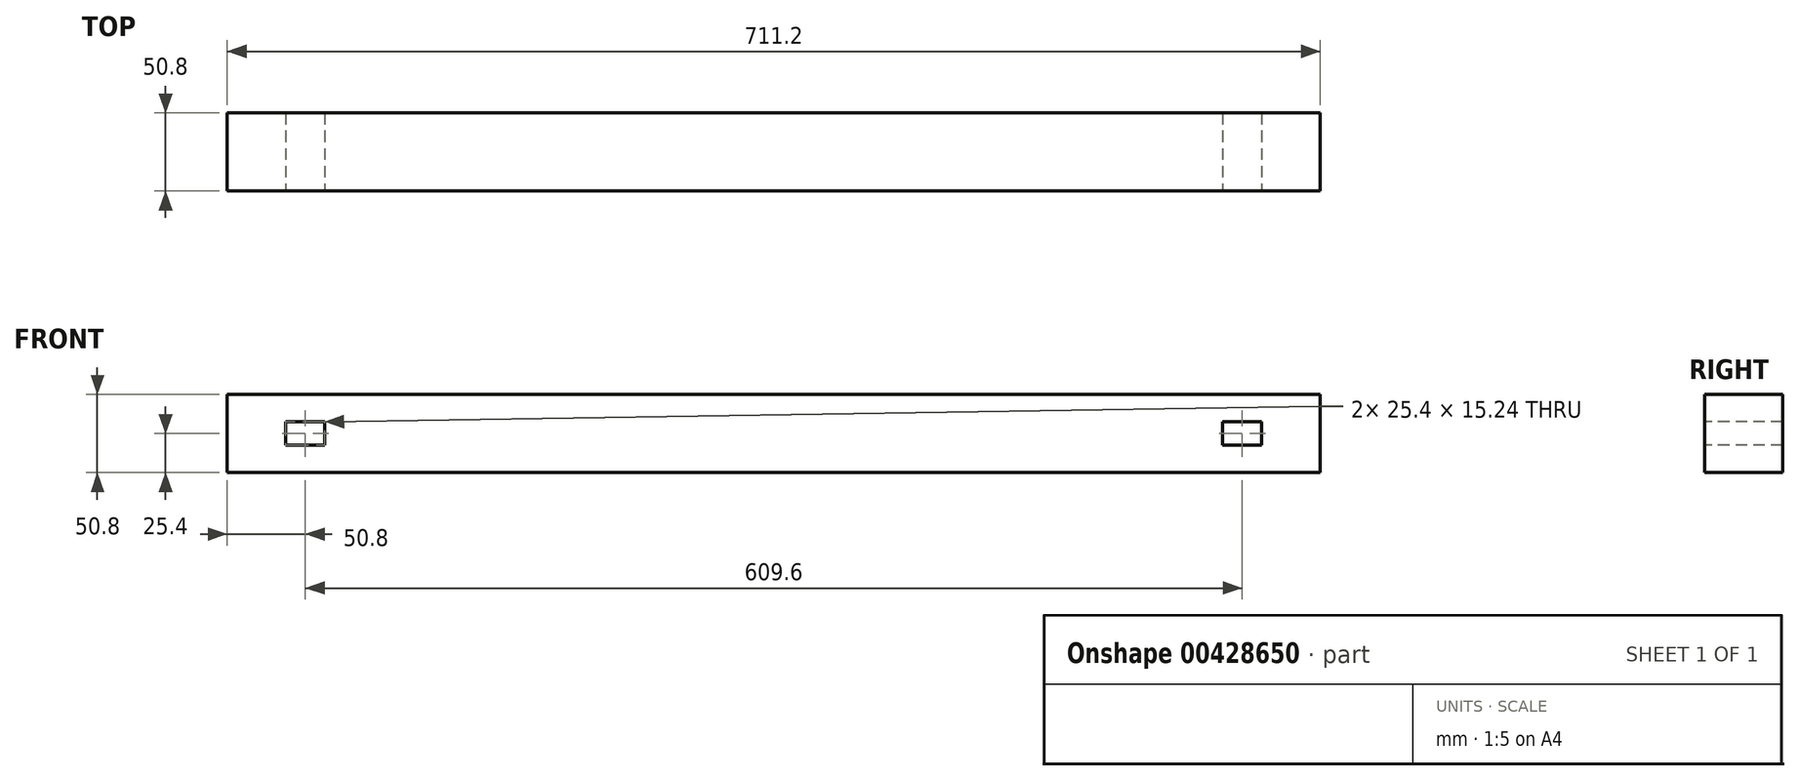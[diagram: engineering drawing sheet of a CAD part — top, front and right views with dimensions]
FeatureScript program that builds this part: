
annotation { "Feature Type Name" : "Feature", "Feature Type Description" : "" }
export const myFeature = defineFeature(function(context is Context, id is Id, definition is map)
    precondition{}
    {
        {
            var Q0;
            Q0=qCreatedBy(makeId("Top.planeOp"),FACE);
            var sketch = newSketch(context, id + "F0", { "sketchPlane" : qUnion([Q0])});
            skLineSegment(sketch, "E0.bottom", {"start": v(-355.6, 25.4) * mm, "end": v(355.6, 25.4) * mm});
            skLineSegment(sketch, "E0.top", {"start": v(-355.6, -25.4) * mm, "end": v(355.6, -25.4) * mm});
            skLineSegment(sketch, "E0.left", {"start": v(-355.6, 25.4) * mm, "end": v(-355.6, -25.4) * mm});
            skLineSegment(sketch, "E0.right", {"start": v(355.6, 25.4) * mm, "end": v(355.6, -25.4) * mm});
            skPoint(sketch, "E0.middle", {"position": v(0, 0) * mm});
            skSolve(sketch);
        }
        {
            var Q0;
            Q0 = qSketchRegion(id + "F0", true);
            extrude(context, id + "F1", {"entities" : qUnion([Q0]), "depth" : 50.8 * mm});
        }
        {
            var Q0;
            Q0=makeQuery(id+"F1.opExtrude","SWEPT_FACE",FACE,{"disambiguationData":[OSD([sQuery(id+"F0.wireOp",EDGE,"E0.top")])]});
            var sketch = newSketch(context, id + "F2", { "sketchPlane" : qUnion([Q0])});
            skLineSegment(sketch, "E1", {"start": v(-355.6, 25.4) * mm, "end": v(-317.5, 25.4) * mm});
            skLineSegment(sketch, "E2", {"start": v(-317.5, 50.8) * mm, "end": v(-317.5, 33.02) * mm});
            skLineSegment(sketch, "E3.bottom", {"start": v(-317.5, 33.02) * mm, "end": v(-292.1, 33.02) * mm});
            skLineSegment(sketch, "E3.top", {"start": v(-317.5, 17.78) * mm, "end": v(-292.1, 17.78) * mm});
            skLineSegment(sketch, "E3.left", {"start": v(-317.5, 33.02) * mm, "end": v(-317.5, 17.78) * mm});
            skLineSegment(sketch, "E3.right", {"start": v(-292.1, 33.02) * mm, "end": v(-292.1, 17.78) * mm});
            skSolve(sketch);
        }
        {
            var Q0;
            Q0 = qSketchRegion(id + "F2", true);
            extrude(context, id + "F3", {"entities" : qUnion([Q0]), "operationType" : NewBodyOperationType.REMOVE, "oppositeDirection" : true, "depth" : 50.8 * mm});
        }
        {
            var Q0;
            Q0=makeQuery(id+"F1.opExtrude","SWEPT_FACE",FACE,{"disambiguationData":[OSD([sQuery(id+"F0.wireOp",EDGE,"E0.top")])]});
            var sketch = newSketch(context, id + "F4", { "sketchPlane" : qUnion([Q0])});
            skPoint(sketch, "E4.endSnap0", {"position": v(355.6, 25.4) * mm});
            skLineSegment(sketch, "E5", {"start": v(355.6, 25.4) * mm, "end": v(317.5, 25.4) * mm});
            skLineSegment(sketch, "E6", {"start": v(317.5, 50.8) * mm, "end": v(317.5, 33.02) * mm});
            skLineSegment(sketch, "E7.bottom", {"start": v(317.5, 33.02) * mm, "end": v(292.1, 33.02) * mm});
            skLineSegment(sketch, "E7.top", {"start": v(317.5, 17.78) * mm, "end": v(292.1, 17.78) * mm});
            skLineSegment(sketch, "E7.left", {"start": v(317.5, 33.02) * mm, "end": v(317.5, 17.78) * mm});
            skLineSegment(sketch, "E7.right", {"start": v(292.1, 33.02) * mm, "end": v(292.1, 17.78) * mm});
            skSolve(sketch);
        }
        {
            var Q0;
            Q0 = qSketchRegion(id + "F4", true);
            extrude(context, id + "F5", {"entities" : qUnion([Q0]), "operationType" : NewBodyOperationType.REMOVE, "oppositeDirection" : true, "depth" : 50.8 * mm});
        }
    });
